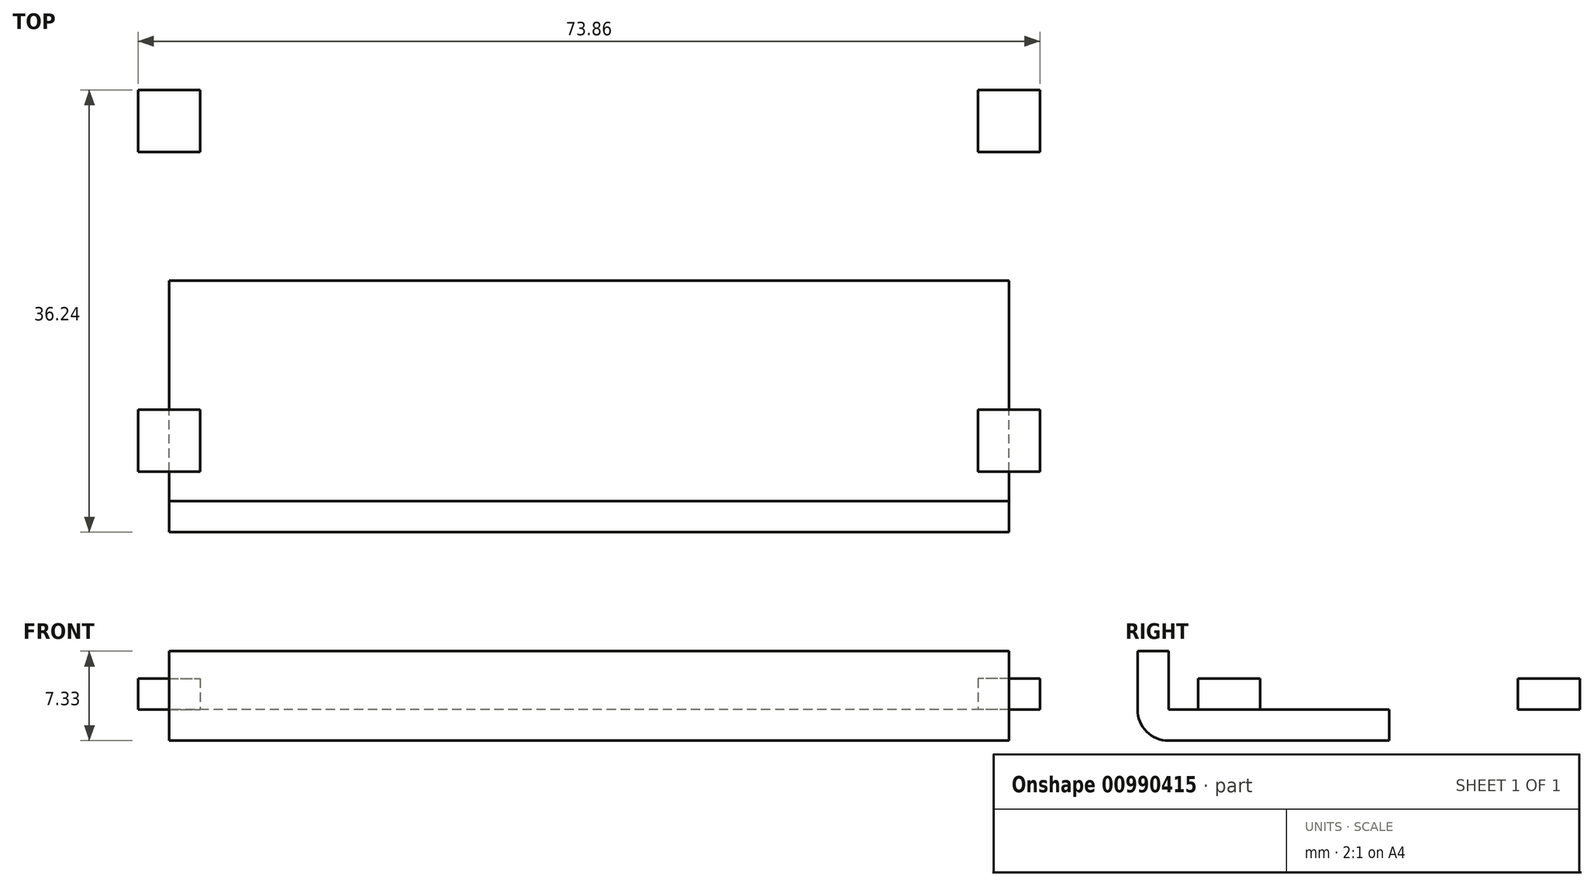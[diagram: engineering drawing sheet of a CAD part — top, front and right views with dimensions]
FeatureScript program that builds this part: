
annotation { "Feature Type Name" : "Feature", "Feature Type Description" : "" }
export const myFeature = defineFeature(function(context is Context, id is Id, definition is map)
    precondition{}
    {
        {
            var Q0;
            Q0=qCreatedBy(makeId("Right.planeOp"),FACE);
            var sketch = newSketch(context, id + "F0", { "sketchPlane" : qUnion([Q0])});
            skLineSegment(sketch, "E0", {"start": v(0, 0) * mm, "end": v(0, 169.34) * mm});
            skLineSegment(sketch, "E1", {"start": v(0, 169.34) * mm, "end": v(200.4, 169.34) * mm});
            skLineSegment(sketch, "E2", {"start": v(0, 0) * mm, "end": v(43.05, 0) * mm, "construction": true});
            skLineSegment(sketch, "E3", {"start": v(43.05, 0) * mm, "end": v(23.47, 45.96) * mm});
            skLineSegment(sketch, "E4", {"start": v(0, 47.82) * mm, "end": v(22.68, 47.82) * mm, "construction": true});
            skLineSegment(sketch, "E5", {"start": v(22.68, 47.82) * mm, "end": v(22.68, 0) * mm, "construction": true});
            skLineSegment(sketch, "E6", {"start": v(23.1, 49.8) * mm, "end": v(40.9, 132) * mm});
            skLineSegment(sketch, "E7", {"start": v(41.4, 134.33) * mm, "end": v(0, 134.33) * mm, "construction": true});
            skLineSegment(sketch, "E8", {"start": v(41.4, 134.33) * mm, "end": v(43.05, 0) * mm, "construction": true});
            skLineSegment(sketch, "E9", {"start": v(43.31, 135.75) * mm, "end": v(72.51, 157.5) * mm});
            skLineSegment(sketch, "E10", {"start": v(74.2, 158.76) * mm, "end": v(74.2, 169.34) * mm, "construction": true});
            skLineSegment(sketch, "E11", {"start": v(74.2, 158.76) * mm, "end": v(0, 158.76) * mm, "construction": true});
            skPoint(sketch, "E12", {"position": v(100.2, 169.34) * mm});
            skLineSegment(sketch, "E13", {"start": v(100.2, 169.34) * mm, "end": v(100.2, 154.3) * mm, "construction": true});
            skLineSegment(sketch, "E14", {"start": v(76.3, 158.76) * mm, "end": v(100.2, 158.76) * mm});
            skLineSegment(sketch, "E15.4", {"start": v(41.18, -0.8) * mm, "end": v(20.56, 47.62) * mm, "construction": true});
            skLineSegment(sketch, "E15.5", {"start": v(20.56, 47.62) * mm, "end": v(39.58, 135.5) * mm});
            skLineSegment(sketch, "E15.6", {"start": v(39.58, 135.5) * mm, "end": v(73.52, 160.79) * mm});
            skLineSegment(sketch, "E15.7", {"start": v(73.52, 160.79) * mm, "end": v(100.2, 160.79) * mm});
            skLineSegment(sketch, "E16.5", {"start": v(11.62, 46.77) * mm, "end": v(31.89, 140.45) * mm});
            skLineSegment(sketch, "E16.6", {"start": v(31.89, 140.45) * mm, "end": v(70.69, 169.35) * mm, "construction": true});
            skLineSegment(sketch, "E16.7", {"start": v(70.69, 169.35) * mm, "end": v(100.2, 169.35) * mm});
            skLineSegment(sketch, "E17", {"start": v(31.89, 140.45) * mm, "end": v(38.14, 169.34) * mm, "construction": true});
            skLineSegment(sketch, "E18", {"start": v(10.6, 158.76) * mm, "end": v(0, 158.76) * mm, "construction": true});
            skLineSegment(sketch, "E19", {"start": v(10.6, 158.76) * mm, "end": v(10.6, 46.77) * mm});
            skLineSegment(sketch, "E20", {"start": v(10.6, 46.77) * mm, "end": v(11.62, 46.77) * mm});
            skLineSegment(sketch, "E21", {"start": v(36.3, 160.79) * mm, "end": v(31.89, 140.45) * mm, "construction": true});
            skLineSegment(sketch, "E22", {"start": v(41.4, 134.33) * mm, "end": v(48.98, 169.34) * mm, "construction": true});
            skLineSegment(sketch, "E23", {"start": v(47.13, 160.79) * mm, "end": v(44.8, 150.07) * mm});
            skLineSegment(sketch, "E24", {"start": v(13.2, 0) * mm, "end": v(0, 0) * mm});
            skLineSegment(sketch, "E25", {"start": v(31.54, 0) * mm, "end": v(43.05, 0) * mm});
            skLineSegment(sketch, "E26", {"start": v(100.2, 158.76) * mm, "end": v(100.2, 169.35) * mm});
            skPoint(sketch, "E27", {"position": v(46.69, 158.76) * mm});
            skPoint(sketch, "E28", {"position": v(56.47, 158.76) * mm});
            skLineSegment(sketch, "E29", {"start": v(46.69, 158.76) * mm, "end": v(56.47, 158.76) * mm});
            skLineSegment(sketch, "E30", {"start": v(44.8, 150.07) * mm, "end": v(46.69, 158.76) * mm});
            skLineSegment(sketch, "E31", {"start": v(10.6, 158.76) * mm, "end": v(35.85, 158.76) * mm});
            skLineSegment(sketch, "E32", {"start": v(35.85, 158.76) * mm, "end": v(31.89, 140.45) * mm});
            skLineSegment(sketch, "E33", {"start": v(44.8, 150.07) * mm, "end": v(56.47, 158.76) * mm});
            skLineSegment(sketch, "E34", {"start": v(30.88, 85.7) * mm, "end": v(20.53, 87.94) * mm, "construction": true});
            skLineSegment(sketch, "E35.0", {"start": v(33.3, -4.15) * mm, "end": v(12.94, 43.67) * mm, "construction": true});
            skLineSegment(sketch, "E36", {"start": v(22.68, 47.82) * mm, "end": v(18.8, 29.9) * mm, "construction": true});
            skLineSegment(sketch, "E37", {"start": v(18.8, 29.9) * mm, "end": v(12.34, 0) * mm});
            skLineSegment(sketch, "E38", {"start": v(18.8, 29.9) * mm, "end": v(31.54, 0) * mm});
            skLineSegment(sketch, "E39", {"start": v(12.34, 0) * mm, "end": v(31.54, 0) * mm});
            skLineSegment(sketch, "E40", {"start": v(20.56, 47.62) * mm, "end": v(40.84, 0) * mm});
            skPoint(sketch, "E41.visualSharp", {"position": v(41.4, 134.33) * mm});
            skArc(sketch, "E41.filletArc", {"start": v(43.31, 135.75) * mm, "mid": v(41.77, 134.1) * mm, "end": v(40.9, 132) * mm});
            skPoint(sketch, "E42.visualSharp", {"position": v(22.68, 47.82) * mm});
            skArc(sketch, "E42.filletArc", {"start": v(23.1, 49.8) * mm, "mid": v(23, 47.85) * mm, "end": v(23.47, 45.96) * mm});
            skPoint(sketch, "E43.visualSharp", {"position": v(74.2, 158.76) * mm});
            skArc(sketch, "E43.filletArc", {"start": v(76.3, 158.76) * mm, "mid": v(74.3, 158.44) * mm, "end": v(72.51, 157.5) * mm});
            skPoint(sketch, "E44", {"position": v(21.75, 93.6) * mm});
            skLineSegment(sketch, "E45", {"start": v(21.75, 93.6) * mm, "end": v(22.1, 95.21) * mm});
            skLineSegment(sketch, "E46", {"start": v(22.1, 95.21) * mm, "end": v(26.54, 94.25) * mm});
            skLineSegment(sketch, "E47", {"start": v(29.56, 96.2) * mm, "end": v(37.5, 132.86) * mm});
            skLineSegment(sketch, "E48", {"start": v(35.55, 135.88) * mm, "end": v(31.1, 136.84) * mm});
            skPoint(sketch, "E49.visualSharp", {"position": v(38.03, 135.35) * mm});
            skArc(sketch, "E49.filletArc", {"start": v(37.5, 132.86) * mm, "mid": v(37.15, 134.78) * mm, "end": v(35.55, 135.88) * mm});
            skPoint(sketch, "E50.visualSharp", {"position": v(29.02, 93.72) * mm});
            skArc(sketch, "E50.filletArc", {"start": v(26.54, 94.25) * mm, "mid": v(28.45, 94.6) * mm, "end": v(29.56, 96.2) * mm});
            skLineSegment(sketch, "E51", {"start": v(21.75, 93.6) * mm, "end": v(32.1, 91.37) * mm, "construction": true});
            skLineSegment(sketch, "E52.0", {"start": v(35.01, 133.4) * mm, "end": v(30.57, 134.36) * mm});
            skLineSegment(sketch, "E52.1", {"start": v(22.64, 97.7) * mm, "end": v(27.08, 96.74) * mm});
            skLineSegment(sketch, "E52.2", {"start": v(27.08, 96.74) * mm, "end": v(27.08, 96.74) * mm});
            skLineSegment(sketch, "E52.3", {"start": v(27.08, 96.74) * mm, "end": v(35.01, 133.4) * mm});
            skLineSegment(sketch, "E52.4", {"start": v(35.01, 133.4) * mm, "end": v(35.01, 133.4) * mm});
            skLineSegment(sketch, "E53.MirrorCS", {"start": v(21.4, 92) * mm, "end": v(25.85, 91.04) * mm});
            skArc(sketch, "E54.MirrorCS", {"start": v(25.85, 91.04) * mm, "mid": v(27.44, 89.94) * mm, "end": v(27.8, 88.02) * mm});
            skLineSegment(sketch, "E55.MirrorCS", {"start": v(27.8, 88.02) * mm, "end": v(19.86, 51.36) * mm});
            skArc(sketch, "E56.MirrorCS", {"start": v(19.86, 51.36) * mm, "mid": v(18.75, 49.76) * mm, "end": v(16.84, 49.41) * mm});
            skLineSegment(sketch, "E57.MirrorCS", {"start": v(16.84, 49.41) * mm, "end": v(12.4, 50.38) * mm});
            skLineSegment(sketch, "E58.MirrorCS", {"start": v(17.37, 51.9) * mm, "end": v(12.94, 52.86) * mm});
            skLineSegment(sketch, "E59.MirrorCS", {"start": v(25.3, 88.56) * mm, "end": v(17.37, 51.9) * mm});
            skLineSegment(sketch, "E60.MirrorCS", {"start": v(20.87, 89.52) * mm, "end": v(25.3, 88.56) * mm});
            skLineSegment(sketch, "E61", {"start": v(33.72, 127.42) * mm, "end": v(31.23, 127.96) * mm});
            skLineSegment(sketch, "E62", {"start": v(31.23, 127.96) * mm, "end": v(30.16, 123) * mm});
            skLineSegment(sketch, "E63", {"start": v(30.16, 123) * mm, "end": v(32.64, 122.46) * mm});
            skLineSegment(sketch, "E64", {"start": v(28.37, 102.7) * mm, "end": v(25.88, 103.24) * mm});
            skLineSegment(sketch, "E65", {"start": v(25.88, 103.24) * mm, "end": v(26.96, 108.2) * mm});
            skLineSegment(sketch, "E66", {"start": v(26.96, 108.2) * mm, "end": v(29.44, 107.66) * mm});
            skLineSegment(sketch, "E67.MirrorCS", {"start": v(24.02, 82.6) * mm, "end": v(21.54, 83.13) * mm});
            skLineSegment(sketch, "E68.MirrorCS", {"start": v(21.54, 83.13) * mm, "end": v(20.46, 78.17) * mm});
            skLineSegment(sketch, "E69.MirrorCS", {"start": v(20.46, 78.17) * mm, "end": v(22.94, 77.63) * mm});
            skLineSegment(sketch, "E70.MirrorCS", {"start": v(17.26, 63.37) * mm, "end": v(19.74, 62.84) * mm});
            skLineSegment(sketch, "E71.MirrorCS", {"start": v(16.19, 58.4) * mm, "end": v(17.26, 63.37) * mm});
            skLineSegment(sketch, "E72.MirrorCS", {"start": v(18.67, 57.87) * mm, "end": v(16.19, 58.4) * mm});
            skLineSegment(sketch, "E73", {"start": v(31.89, 140.45) * mm, "end": v(41.4, 134.33) * mm, "construction": true});
            skLineSegment(sketch, "E74.MirrorCS", {"start": v(37.56, 139.02) * mm, "end": v(34.85, 142.66) * mm});
            skArc(sketch, "E75.MirrorCS", {"start": v(41.12, 138.5) * mm, "mid": v(39.23, 138.02) * mm, "end": v(37.56, 139.02) * mm});
            skLineSegment(sketch, "E76.MirrorCS", {"start": v(71.2, 160.9) * mm, "end": v(41.12, 138.5) * mm});
            skArc(sketch, "E77.MirrorCS", {"start": v(71.72, 164.46) * mm, "mid": v(72.2, 162.57) * mm, "end": v(71.2, 160.9) * mm});
            skLineSegment(sketch, "E78.MirrorCS", {"start": v(69, 168.1) * mm, "end": v(71.72, 164.46) * mm});
            skLineSegment(sketch, "E79.MirrorCS", {"start": v(66.97, 166.58) * mm, "end": v(69.69, 162.94) * mm});
            skLineSegment(sketch, "E80.MirrorCS", {"start": v(69.69, 162.94) * mm, "end": v(39.6, 140.53) * mm});
            skLineSegment(sketch, "E81.MirrorCS", {"start": v(64.8, 159.3) * mm, "end": v(63.28, 161.33) * mm});
            skLineSegment(sketch, "E82.MirrorCS", {"start": v(63.28, 161.33) * mm, "end": v(59.2, 158.3) * mm});
            skLineSegment(sketch, "E83.MirrorCS", {"start": v(59.2, 158.3) * mm, "end": v(60.72, 156.26) * mm});
            skLineSegment(sketch, "E84.MirrorCS", {"start": v(47.06, 149.26) * mm, "end": v(48.58, 147.22) * mm});
            skLineSegment(sketch, "E85.MirrorCS", {"start": v(42.99, 146.22) * mm, "end": v(47.06, 149.26) * mm});
            skLineSegment(sketch, "E86.MirrorCS", {"start": v(44.5, 144.19) * mm, "end": v(42.99, 146.22) * mm});
            skLineSegment(sketch, "E87.MirrorCS", {"start": v(39.6, 140.53) * mm, "end": v(36.89, 144.18) * mm});
            skLineSegment(sketch, "E88", {"start": v(70.69, 169.35) * mm, "end": v(70.69, 164.55) * mm});
            skPoint(sketch, "E89.visualSharp", {"position": v(70.69, 162) * mm});
            skArc(sketch, "E89.filletArc", {"start": v(68.15, 162) * mm, "mid": v(69.94, 162.75) * mm, "end": v(70.69, 164.55) * mm});
            skLineSegment(sketch, "E90.1", {"start": v(68.15, 169.63) * mm, "end": v(68.15, 164.55) * mm});
            skLineSegment(sketch, "E91", {"start": v(55.17, 164.55) * mm, "end": v(55.17, 167.09) * mm});
            skLineSegment(sketch, "E92", {"start": v(55.17, 167.09) * mm, "end": v(50.1, 167.09) * mm});
            skLineSegment(sketch, "E93", {"start": v(50.1, 167.09) * mm, "end": v(50.1, 164.55) * mm});
            skLineSegment(sketch, "E94", {"start": v(28.37, 164.55) * mm, "end": v(28.37, 167.09) * mm});
            skLineSegment(sketch, "E95", {"start": v(28.37, 167.09) * mm, "end": v(23.3, 167.09) * mm});
            skLineSegment(sketch, "E96", {"start": v(23.3, 167.09) * mm, "end": v(23.3, 164.55) * mm});
            skLineSegment(sketch, "E97", {"start": v(22.68, 47.82) * mm, "end": v(11.62, 46.77) * mm, "construction": true});
            skLineSegment(sketch, "E98", {"start": v(15.36, 37.97) * mm, "end": v(19.78, 39.85) * mm});
            skLineSegment(sketch, "E99", {"start": v(23.11, 38.51) * mm, "end": v(37.3, 5.2) * mm});
            skLineSegment(sketch, "E100", {"start": v(35.96, 1.87) * mm, "end": v(31.54, -0.01) * mm});
            skPoint(sketch, "E101.visualSharp", {"position": v(38.3, 2.87) * mm});
            skArc(sketch, "E101.filletArc", {"start": v(35.96, 1.87) * mm, "mid": v(37.32, 3.26) * mm, "end": v(37.3, 5.2) * mm});
            skPoint(sketch, "E102.visualSharp", {"position": v(22.12, 40.85) * mm});
            skArc(sketch, "E102.filletArc", {"start": v(23.11, 38.51) * mm, "mid": v(21.72, 39.87) * mm, "end": v(19.78, 39.85) * mm});
            skLineSegment(sketch, "E103.0", {"start": v(34.97, 4.2) * mm, "end": v(25.52, 0.18) * mm});
            skLineSegment(sketch, "E103.1", {"start": v(20.78, 37.52) * mm, "end": v(34.97, 4.2) * mm});
            skLineSegment(sketch, "E103.2", {"start": v(16.36, 35.63) * mm, "end": v(20.78, 37.52) * mm});
            skLineSegment(sketch, "E104", {"start": v(27.86, 20.9) * mm, "end": v(25.52, 19.9) * mm});
            skLineSegment(sketch, "E105", {"start": v(25.52, 19.9) * mm, "end": v(23.53, 24.57) * mm});
            skLineSegment(sketch, "E106", {"start": v(23.53, 24.57) * mm, "end": v(25.87, 25.57) * mm});
            skLineSegment(sketch, "E107", {"start": v(21.48, 35.85) * mm, "end": v(19.15, 34.86) * mm});
            skLineSegment(sketch, "E108", {"start": v(19.15, 34.86) * mm, "end": v(21.14, 30.18) * mm});
            skLineSegment(sketch, "E109", {"start": v(21.14, 30.18) * mm, "end": v(23.48, 31.18) * mm});
            skLineSegment(sketch, "E110", {"start": v(79.6, 169.35) * mm, "end": v(79.6, 164.55) * mm});
            skLineSegment(sketch, "E111", {"start": v(82.14, 162) * mm, "end": v(100.2, 162) * mm});
            skPoint(sketch, "E112.visualSharp", {"position": v(79.6, 162) * mm});
            skArc(sketch, "E112.filletArc", {"start": v(79.6, 164.55) * mm, "mid": v(80.34, 162.75) * mm, "end": v(82.14, 162) * mm});
            skLineSegment(sketch, "E113.0", {"start": v(82.14, 164.55) * mm, "end": v(100.2, 164.55) * mm});
            skLineSegment(sketch, "E113.1", {"start": v(82.14, 169.35) * mm, "end": v(82.14, 164.55) * mm});
            skLineSegment(sketch, "E114", {"start": v(84.57, 164.55) * mm, "end": v(84.57, 167.09) * mm});
            skPoint(sketch, "E114.endSnap0", {"position": v(68.15, 167.09) * mm});
            skLineSegment(sketch, "E115", {"start": v(84.57, 167.09) * mm, "end": v(89.65, 167.09) * mm});
            skLineSegment(sketch, "E116", {"start": v(89.65, 167.09) * mm, "end": v(89.65, 164.55) * mm});
            skLineSegment(sketch, "E117", {"start": v(10.6, 158.76) * mm, "end": v(10.6, 164.55) * mm, "construction": true});
            skLineSegment(sketch, "E118", {"start": v(68.15, 164.55) * mm, "end": v(18.21, 164.55) * mm});
            skLineSegment(sketch, "E119", {"start": v(68.15, 162) * mm, "end": v(18.21, 162) * mm});
            skLineSegment(sketch, "E120", {"start": v(18.21, 164.55) * mm, "end": v(18.21, 169.34) * mm});
            skLineSegment(sketch, "E121", {"start": v(15.67, 164.55) * mm, "end": v(15.67, 169.34) * mm});
            skPoint(sketch, "E122.visualSharp", {"position": v(15.67, 162) * mm});
            skArc(sketch, "E122.filletArc", {"start": v(15.67, 164.55) * mm, "mid": v(16.42, 162.75) * mm, "end": v(18.21, 162) * mm});
            skLineSegment(sketch, "E123", {"start": v(15.67, 164.55) * mm, "end": v(18.21, 164.55) * mm, "construction": true});
            skLineSegment(sketch, "E124", {"start": v(10.6, 164.55) * mm, "end": v(15.67, 164.55) * mm, "construction": true});
            skLineSegment(sketch, "E125", {"start": v(23.3, 165.82) * mm, "end": v(18.21, 165.82) * mm, "construction": true});
            skLineSegment(sketch, "E126.MirrorCS", {"start": v(118.27, 164.55) * mm, "end": v(100.2, 164.55) * mm});
            skLineSegment(sketch, "E127.MirrorCS", {"start": v(110.76, 167.09) * mm, "end": v(110.76, 164.55) * mm});
            skLineSegment(sketch, "E128.MirrorCS", {"start": v(115.84, 167.09) * mm, "end": v(110.76, 167.09) * mm});
            skLineSegment(sketch, "E129.MirrorCS", {"start": v(115.84, 164.55) * mm, "end": v(115.84, 167.09) * mm});
            skLineSegment(sketch, "E130.MirrorCS", {"start": v(118.27, 169.35) * mm, "end": v(118.27, 164.55) * mm});
            skLineSegment(sketch, "E131.MirrorCS", {"start": v(120.8, 169.35) * mm, "end": v(120.8, 164.55) * mm});
            skArc(sketch, "E132.MirrorCS", {"start": v(120.8, 164.55) * mm, "mid": v(120.06, 162.75) * mm, "end": v(118.27, 162) * mm});
            skLineSegment(sketch, "E133.MirrorCS", {"start": v(118.27, 162) * mm, "end": v(100.2, 162) * mm});
            skSolve(sketch);
        }
        {
            var Q0;
            {var subQ0=sQuery(id+"F0.wireOp",EDGE,"E111");Q0=makeQuery(id+"F0.imprint","IMPRINT",FACE,{"disambiguationData":[TD([[makeQuery(id+"F0.imprint","IMPRINT",EDGE,{"derivedFrom":subQ0}),1.0]])]});}
            var Q1;
            {var subQ12=sQuery(id+"F0.wireOp",EDGE,"E132.MirrorCS");Q1=makeQuery(id+"F0.imprint","IMPRINT",FACE,{"disambiguationData":[TD([[makeQuery(id+"F0.imprint","IMPRINT",EDGE,{"derivedFrom":subQ12}),-1.0]])]});}
            extrude(context, id + "F1", {"entities" : qUnion([Q0, Q1]), "endBound" : BoundingType.SYMMETRIC, "depth" : 68.78 * mm, "offsetDistance" : 25.4 * mm});
        }
        {
            var Q0;
            {var subQ0=sQuery(id+"F0.wireOp",EDGE,"E114");Q0=makeQuery(id+"F0.imprint","IMPRINT",FACE,{"disambiguationData":[TD([[makeQuery(id+"F0.imprint","IMPRINT",EDGE,{"derivedFrom":subQ0}),-1.0]])]});}
            var Q1;
            {var subQ0=sQuery(id+"F0.wireOp",EDGE,"E127.MirrorCS");Q1=makeQuery(id+"F0.imprint","IMPRINT",FACE,{"disambiguationData":[TD([[makeQuery(id+"F0.imprint","IMPRINT",EDGE,{"derivedFrom":subQ0}),1.0]])]});}
            extrude(context, id + "F2", {"entities" : qUnion([Q0, Q1]), "operationType" : NewBodyOperationType.ADD, "surfaceOperationType" : NewSurfaceOperationType.ADD, "depth" : 36.93 * mm, "offsetDistance" : 25.4 * mm, "hasSecondDirection" : true, "secondDirectionOppositeDirection" : true, "secondDirectionDepth" : -31.85 * mm});
        }
        {
            var Q0;
            {var subQ0=sQuery(id+"F0.wireOp",EDGE,"E114");Q0=makeQuery(id+"F0.imprint","IMPRINT",FACE,{"disambiguationData":[TD([[makeQuery(id+"F0.imprint","IMPRINT",EDGE,{"derivedFrom":subQ0}),-1.0]])]});}
            var Q1;
            {var subQ0=sQuery(id+"F0.wireOp",EDGE,"E127.MirrorCS");Q1=makeQuery(id+"F0.imprint","IMPRINT",FACE,{"disambiguationData":[TD([[makeQuery(id+"F0.imprint","IMPRINT",EDGE,{"derivedFrom":subQ0}),1.0]])]});}
            extrude(context, id + "F3", {"entities" : qUnion([Q0, Q1]), "operationType" : NewBodyOperationType.ADD, "depth" : -36.93 * mm, "offsetDistance" : 25.4 * mm, "hasSecondDirection" : true, "secondDirectionOppositeDirection" : true, "secondDirectionDepth" : 31.85 * mm});
        }
    });
